# Revit family: Haworth_Lotus_Chair_Medium
name_source: partatom
category: Furniture
revit_build: Autodesk Revit 2018 (Build: 20170223_1515(x64)
units: mm (PartAtom-declared; Revit-internal decimal feet)

## family parameters
Always vertical = Yes
Cut with Voids When Loaded = No
OmniClass Number = 23.40.70.14.64.11
OmniClass Title = Office Furniture
Room Calculation Point = No
Shared = No
Work Plane-Based = No

## types (4) — shared parameters
Arm Height = 16.4018 "
Assembly Code = E2020200
Base Finish = Haworth _ Metal _ Chrome
Description = Haworth Lotus Chair Medium
Hardware Finish = Haworth _ Paint _ Black
Manufacturer = Haworth
Model = HCCE-LTUM
Revision Number = 4
URL = http://www.haworth.com
URL - Product = http://www.haworth.com
Warranty = http://www.haworth.com

## per-type parameters (varying)
| type | Five Star Base | Four Star Base | With Arms | Without Arms |
| HCCE-LTUM - Four Spoke Base - With Arms | No | Yes | Yes | No |
| HCCE-LTUM - Four Spoke Base - Without Arms | No | Yes | No | Yes |
| HCCE-LTUM - Five Spoke Base - With Arms | Yes | No | Yes | No |
| HCCE-LTUM - Five Spoke Base - Without Arms | Yes | No | No | Yes |

## geometry (parser evidence)
native form markers: Sweep x17
no freeform markers — native parametric forms only
